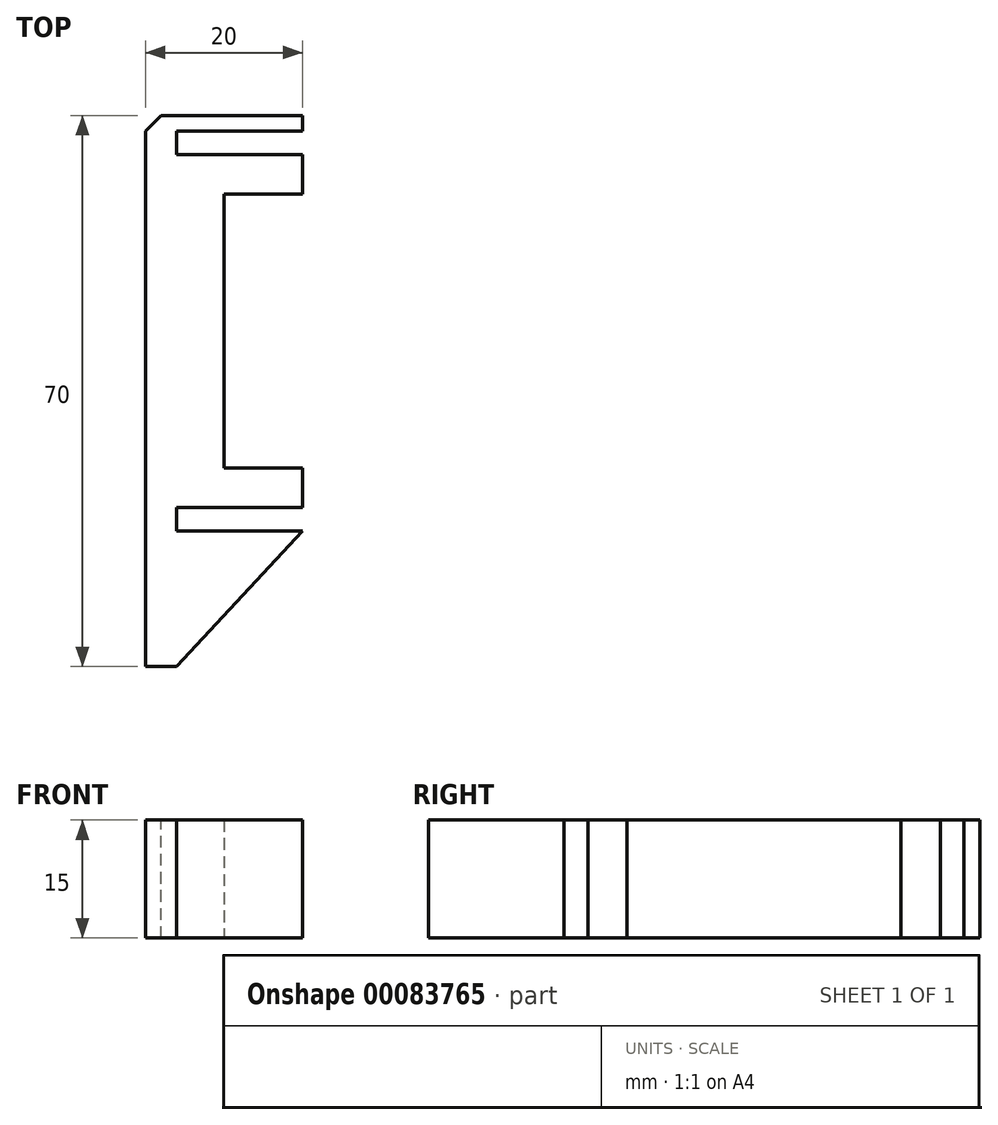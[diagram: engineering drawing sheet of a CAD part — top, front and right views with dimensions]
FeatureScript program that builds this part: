
annotation { "Feature Type Name" : "Feature", "Feature Type Description" : "" }
export const myFeature = defineFeature(function(context is Context, id is Id, definition is map)
    precondition{}
    {
        {
            var Q0;
            Q0=qCreatedBy(makeId("Top.planeOp"),FACE);
            var sketch = newSketch(context, id + "F0", { "sketchPlane" : qUnion([Q0])});
            skLineSegment(sketch, "E0", {"start": v(0, 70) * mm, "end": v(0, 0) * mm});
            skLineSegment(sketch, "E1", {"start": v(0, 0) * mm, "end": v(4, 0) * mm});
            skLineSegment(sketch, "E2", {"start": v(4, 0) * mm, "end": v(20, 17.2) * mm});
            skLineSegment(sketch, "E3", {"start": v(20, 17.2) * mm, "end": v(4, 17.2) * mm});
            skLineSegment(sketch, "E4", {"start": v(4, 17.2) * mm, "end": v(4, 20.2) * mm});
            skLineSegment(sketch, "E5", {"start": v(4, 20.2) * mm, "end": v(20, 20.2) * mm});
            skLineSegment(sketch, "E6", {"start": v(20, 20.2) * mm, "end": v(20, 25.2) * mm});
            skLineSegment(sketch, "E7", {"start": v(20, 25.2) * mm, "end": v(10, 25.2) * mm});
            skLineSegment(sketch, "E8", {"start": v(10, 25.2) * mm, "end": v(10, 60) * mm});
            skLineSegment(sketch, "E9", {"start": v(10, 60) * mm, "end": v(20, 60) * mm});
            skLineSegment(sketch, "E10", {"start": v(20, 60) * mm, "end": v(20, 65) * mm});
            skLineSegment(sketch, "E11", {"start": v(20, 65) * mm, "end": v(4, 65) * mm});
            skLineSegment(sketch, "E12", {"start": v(4, 65) * mm, "end": v(4, 68) * mm});
            skLineSegment(sketch, "E13", {"start": v(4, 68) * mm, "end": v(20, 68) * mm});
            skLineSegment(sketch, "E14", {"start": v(20, 68) * mm, "end": v(20, 70) * mm});
            skLineSegment(sketch, "E15", {"start": v(20, 70) * mm, "end": v(0, 70) * mm});
            skSolve(sketch);
        }
        {
            var Q0;
            Q0 = qSketchRegion(id + "F0", true);
            extrude(context, id + "F1", {"entities" : qUnion([Q0]), "depth" : 15 * mm});
        }
        {
            var Q0;
            Q0=makeQuery(id+"F1.opExtrude","SWEPT_EDGE",EDGE,{"disambiguationData":[OSD([sQuery(id+"F0.wireOp",EDGE,"E0"),sQuery(id+"F0.wireOp",EDGE,"E15")])]});
            chamfer(context, id + "F2", {"entities" : qUnion([Q0]), "width" : 2 * mm, "tangentPropagation" : true});
        }
    });
